# Revit family: TH5015551_Grifería para Lavaplatos Monocontrol Thames
name_source: partatom
category: Plumbing Fixtures
units: mm (PartAtom-declared; Revit-internal decimal feet)

## family parameters
Always vertical = Yes
Cut with Voids When Loaded = No
OmniClass Number = 23.21.21.19
OmniClass Title = Commercial Dishwasher Equipment
Part Type = Normal
Room Calculation Point = No
Round Connector Dimension = Use Diameter
Shared = No
Work Plane-Based = No

## types (1)
- TH5015551_Grifería para Lavaplatos Monocontrol Thames
    Acabado = Cromado
    Alto = 32.1 cm
    Ancho = 5 cm
    Capacidad de flujo = 7.62 l/m máximo a 60 psi
    Colección = Vida 2016
    Consumo de agua = 7.62 lt
    Creado por = IDD
    Description = Pide ahora esta grifería atractiva, funcional y elegante. ¡Un elemento de diseño que por sí solo deslumbra en la cocina!
    Fecha de creación = 22/04/2020
    Garantía = 30 años en estructura
    Garantías de otros componentes = 5 años en acabados
    Incluye = Cuerpo, pico, manija
    Largo = 18.5 cm
    Línea = Thames
    Material = Corona_Plastico_Cromado
    Materiales = Polímero de alta ingeniería
    Productos compatibles = Lavaplatos
    Rango de presión de agua = Entre 20 y 125 psi
    Resistencia = Resistente a la corrosión pelado y decoloración por agua
    Sistema de accionamiento = Palanca
    Tecnologías = DuraCrome
    Temperatura de uso = Entre 4˚C y 66˚C
    Tipo de chorro = Espumoso
    Tipo de grifería = Monocontrol
    Tipo de manija/accionamiento = Palanca
    URL = https://corona.co
    Uso = Residencial

## geometry (parser evidence)
native form markers: Sweep x5
no freeform markers — native parametric forms only
